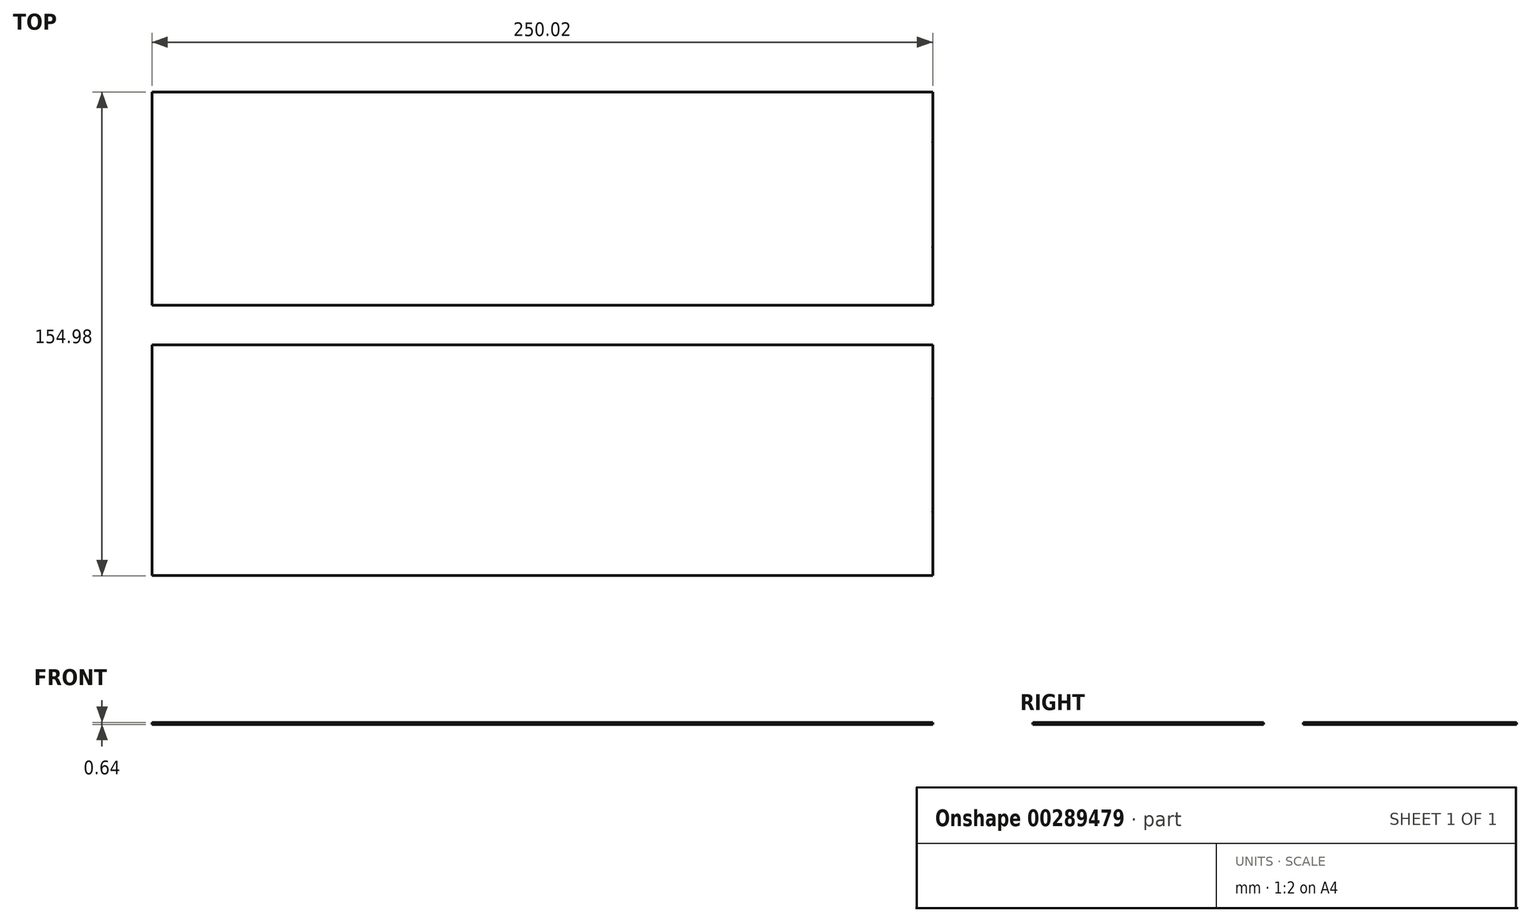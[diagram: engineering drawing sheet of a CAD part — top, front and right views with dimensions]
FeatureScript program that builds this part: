
annotation { "Feature Type Name" : "Feature", "Feature Type Description" : "" }
export const myFeature = defineFeature(function(context is Context, id is Id, definition is map)
    precondition{}
    {
        {
            var Q0;
            Q0=qCreatedBy(makeId("Top.planeOp"),FACE);
            var sketch = newSketch(context, id + "F0", { "sketchPlane" : qUnion([Q0])});
            skLineSegment(sketch, "E0.bottom", {"start": v(125, 34.16) * mm, "end": v(-125, 34.16) * mm});
            skLineSegment(sketch, "E0.top", {"start": v(125, -34.16) * mm, "end": v(-125, -34.16) * mm});
            skLineSegment(sketch, "E0.left", {"start": v(125, 34.16) * mm, "end": v(125, -34.16) * mm});
            skLineSegment(sketch, "E0.right", {"start": v(-125, 34.16) * mm, "end": v(-125, -34.16) * mm});
            skPoint(sketch, "E0.middle", {"position": v(0, 0) * mm});
            skPoint(sketch, "E1", {"position": v(125, -15.57) * mm});
            skPoint(sketch, "E2", {"position": v(125, 18.1) * mm});
            skPoint(sketch, "E3.MirrorP", {"position": v(-125, 18.1) * mm});
            skPoint(sketch, "E4.MirrorP", {"position": v(-125, -15.57) * mm});
            skSolve(sketch);
        }
        {
            var Q0;
            Q0 = qSketchRegion(id + "F0", true);
            extrude(context, id + "F1", {"entities" : qUnion([Q0]), "depth" : 0.64 * mm});
        }
        {
            var Q0;
            Q0=qCreatedBy(makeId("Top.planeOp"),FACE);
            var sketch = newSketch(context, id + "F2", { "sketchPlane" : qUnion([Q0])});
            skLineSegment(sketch, "E5.bottom", {"start": v(-125, -46.86) * mm, "end": v(125, -46.86) * mm});
            skLineSegment(sketch, "E5.top", {"start": v(-125, -120.82) * mm, "end": v(125, -120.82) * mm});
            skLineSegment(sketch, "E5.left", {"start": v(-125, -46.86) * mm, "end": v(-125, -120.82) * mm});
            skLineSegment(sketch, "E5.right", {"start": v(125, -46.86) * mm, "end": v(125, -120.82) * mm});
            skPoint(sketch, "E5.middle", {"position": v(0, -83.84) * mm});
            skPoint(sketch, "E6", {"position": v(125, -100.32) * mm});
            skPoint(sketch, "E7", {"position": v(125, -64.1) * mm});
            skPoint(sketch, "E8.MirrorP", {"position": v(-125, -64.1) * mm});
            skPoint(sketch, "E9.MirrorP", {"position": v(-125, -100.32) * mm});
            skSolve(sketch);
        }
        {
            var Q0;
            Q0 = qSketchRegion(id + "F2", true);
            extrude(context, id + "F3", {"entities" : qUnion([Q0]), "depth" : 0.64 * mm});
        }
        {
            var Q0;
            Q0=sQuery(id+"F0.wireOp",VERTEX,"E3.MirrorP");
            var Q1;
            Q1=sQuery(id+"F0.wireOp",VERTEX,"E4.MirrorP");
            var Q2;
            Q2=sQuery(id+"F2.wireOp",VERTEX,"E8.MirrorP");
            var Q3;
            Q3=sQuery(id+"F2.wireOp",VERTEX,"E9.MirrorP");
            var Q4;
            Q4=sQuery(id+"F2.wireOp",VERTEX,"E6");
            var Q5;
            Q5=sQuery(id+"F2.wireOp",VERTEX,"E7");
            var Q6;
            Q6=sQuery(id+"F0.wireOp",VERTEX,"E1");
            var Q7;
            Q7=sQuery(id+"F0.wireOp",VERTEX,"E2");
            var Q8;
            Q8=makeQuery(id+"F1.opExtrude","SWEPT_BODY",BODY,{"disambiguationData":[OSD([sQuery(id+"F0.wireOp",EDGE,"E0.bottom"),sQuery(id+"F0.wireOp",EDGE,"E0.top"),sQuery(id+"F0.wireOp",EDGE,"E0.left"),sQuery(id+"F0.wireOp",EDGE,"E0.right")])]});
            var Q9;
            Q9=makeQuery(id+"F3.opExtrude","SWEPT_BODY",BODY,{"disambiguationData":[OSD([sQuery(id+"F2.wireOp",EDGE,"E5.bottom"),sQuery(id+"F2.wireOp",EDGE,"E5.top"),sQuery(id+"F2.wireOp",EDGE,"E5.left"),sQuery(id+"F2.wireOp",EDGE,"E5.right")])]});
            hole(context, id + "F4", {"style" : HoleStyle.SIMPLE, "endStyle" : HoleEndStyle.THROUGH, "oppositeDirection" : true, "holeDiameter" : 0.13 * mm, "tappedDepth" : 12.7 * mm, "tapClearance" : 3, "locations" : qUnion([Q0, Q1, Q2, Q3, Q4, Q5, Q6, Q7]), "scope" : qUnion([Q8, Q9]), "startStyle" : HoleStartStyle.PART});
        }
    });
